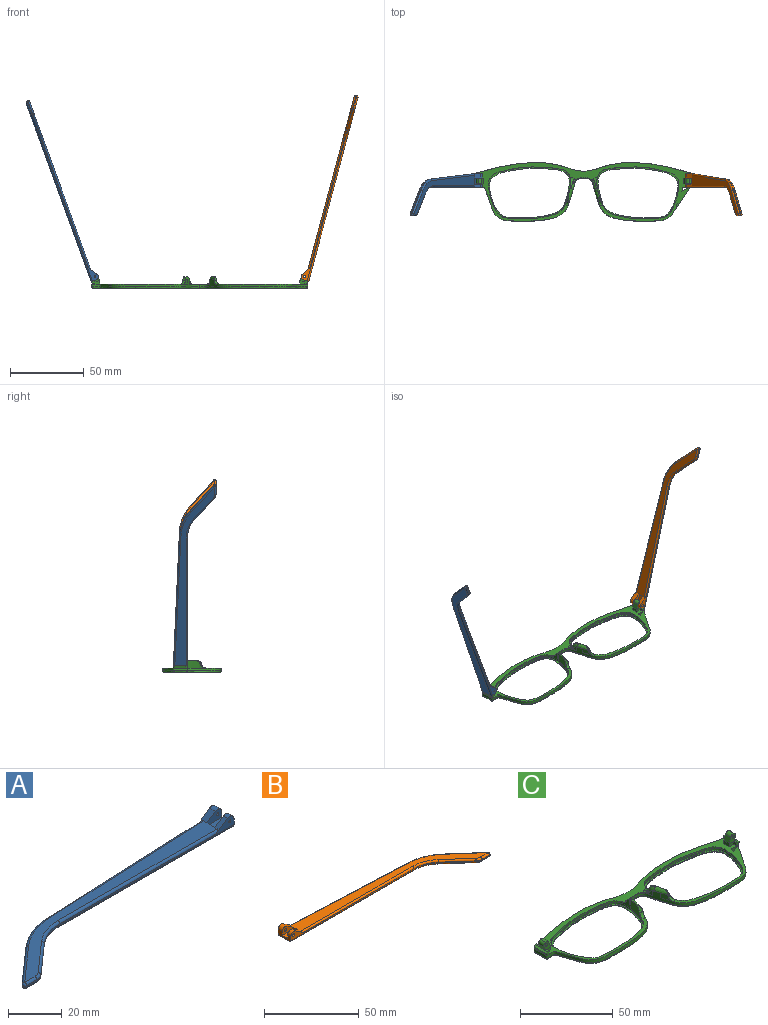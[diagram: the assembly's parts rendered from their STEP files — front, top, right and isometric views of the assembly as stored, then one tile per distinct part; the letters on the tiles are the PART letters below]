
ASSEMBLY  parts=3 mates=2
PART A: 43 faces, bbox 130.2x29.5x5.9 mm
  f0: plane 9.62x3.72mm, normal (1,0,0), area 24.7mm2, adj f1,f3,f4,f5,f10,f16,f18,f28
  f1: cylinder r=2.2mm len=3.45mm, axis (0,-1,0), area 11mm2, adj f0,f2,f4,f37
  f2: plane 6.01x3.91mm, normal (-0.55,0,0.84), area 12.7mm2, adj f1,f4,f9,f19,f37
  f3: plane 2.26x0.1mm, normal (0,0,1), area 0.1mm2, adj f0,f5,f18
  f4: plane 92.1x4.9mm, normal (0,-1,0), area 79.9mm2, adj f0,f1,f2,f14,f19,f36,f42
  f5: plane 93.42x4.13mm, normal (-0.04,1,0), area 64.8mm2, adj f0,f3,f11,f15,f17,f27,f28
  f6: plane 17.82x15.72mm, normal (-0.66,0.75,0), area 14.3mm2, adj f11,f12,f25,f30
  f7: plane 5.46x0.6mm, normal (0,-1,0), area 3.3mm2, adj f12,f13,f23,f32
  f8: plane 14.99x13.23mm, normal (0.66,-0.75,0), area 12mm2, adj f13,f14,f21,f34
  f9: plane 121.18x26.73mm, normal (0,0,1), area 627.7mm2, adj f2,f17,f19,f20,f21,f22,f23,f25
  f10: plane 129.1x27.08mm, normal (0,0,-1), area 686.5mm2, adj f0,f28,f29,f30,f32,f33,f34,f35
  f11: cylinder r=30mm len=18.52mm, axis (0,0,-1), area 12.2mm2, adj f5,f6,f26,f29
  f12: cylinder r=1mm len=1.75mm, axis (0,0,-1), area 1.5mm2, adj f6,f7,f24,f31
  f13: cylinder r=5mm len=3.31mm, axis (0,0,-1), area 2.2mm2, adj f7,f8,f22,f33
  f14: cylinder r=20mm len=13.23mm, axis (0,0,1), area 8.7mm2, adj f4,f8,f20,f35
  f15: plane 5.66x0.25mm, normal (0,0,-1), area 0.7mm2, adj f5,f17,f18
  f16: cylinder r=2.2mm len=3.45mm, axis (0,-1,0), area 14.8mm2, adj f0,f17,f18,f38
  f17: plane 6.01x3.91mm, normal (-0.55,0,0.84), area 16.9mm2, adj f5,f9,f15,f16,f18,f27,f38
  f18: plane 7.92x3.3mm, normal (0,1,0), area 15.9mm2, adj f0,f3,f15,f16,f17,f41
  f19: cylinder r=1mm len=84.18mm, axis (-1,0,0), area 131.4mm2, adj f2,f4,f9,f20
  f20: torus R=21mm, axis (0,0,1), area 23.1mm2, adj f9,f14,f19,f21
  f21: cylinder r=1mm len=15.65mm, axis (-0.75,-0.66,0), area 31.4mm2, adj f8,f9,f20,f22
  f22: torus R=4mm, axis (0,0,1), area 5.3mm2, adj f9,f13,f21,f23
  f23: cylinder r=1mm len=5.46mm, axis (-1,0,0), area 8.6mm2, adj f7,f9,f22,f24
  f24: sphere r=1mm, area 2.4mm2, adj f12,f23,f25
  f25: cylinder r=1mm len=18.48mm, axis (0.75,0.66,0), area 37.3mm2, adj f6,f9,f24,f26
  f26: torus R=29mm, axis (0,0,1), area 31.6mm2, adj f9,f11,f25,f27
  f27: cylinder r=1mm len=85.5mm, axis (1,0.04,0), area 133.5mm2, adj f5,f9,f17,f26
  f28: cylinder r=1mm len=93.46mm, axis (-1,-0.04,0), area 146.9mm2, adj f0,f5,f10,f29
  f29: torus R=29mm, axis (0,0,1), area 31.6mm2, adj f10,f11,f28,f30
  f30: cylinder r=1mm len=18.48mm, axis (-0.75,-0.66,0), area 37.3mm2, adj f6,f10,f29,f31
  f31: sphere r=1mm, area 2.4mm2, adj f12,f30,f32
  f32: cylinder r=1mm len=5.46mm, axis (1,0,0), area 8.6mm2, adj f7,f10,f31,f33
  f33: torus R=4mm, axis (0,0,1), area 5.3mm2, adj f10,f13,f32,f34
  f34: cylinder r=1mm len=15.65mm, axis (0.75,0.66,0), area 31.4mm2, adj f8,f10,f33,f35
  f35: torus R=21mm, axis (0,0,1), area 23.1mm2, adj f10,f14,f34,f36
  f36: cylinder r=1mm len=92.1mm, axis (1,0,0), area 144.7mm2, adj f0,f4,f10,f35
  f37: plane 7.92x4.7mm, normal (0,1,0), area 27mm2, adj f0,f1,f2,f39,f40,f42
  f38: plane 7.92x4.7mm, normal (0,-1,0), area 27mm2, adj f0,f16,f17,f39,f40,f41
  f39: plane 7.92x4.1mm, normal (0,0,1), area 32.5mm2, adj f0,f37,f38,f40
  f40: plane 4.1x1.4mm, normal (1,0,0), area 5.7mm2, adj f9,f37,f38,f39
  f41: cylinder r=0.5mm len=3.1mm, axis (0,-1,0), area 9.7mm2, adj f18,f38
  f42: cylinder r=0.5mm len=2.3mm, axis (0,-1,0), area 7.2mm2, adj f4,f37
PART B: 43 faces, bbox 130.2x29.5x5.9 mm
  f0: plane 9.62x3.72mm, normal (-1,0,0), area 24.7mm2, adj f1,f3,f4,f5,f10,f16,f18,f28
  f1: cylinder r=2.2mm len=3.45mm, axis (0,-1,0), area 11mm2, adj f0,f2,f4,f37
  f2: plane 6.01x3.91mm, normal (0.55,0,0.84), area 12.7mm2, adj f1,f4,f9,f19,f37
  f3: plane 2.26x0.1mm, normal (0,0,1), area 0.1mm2, adj f0,f5,f18
  f4: plane 92.1x4.9mm, normal (0,-1,0), area 78.2mm2, adj f0,f1,f2,f14,f19,f36,f42
  f5: plane 93.42x4.13mm, normal (0.04,1,0), area 64.8mm2, adj f0,f3,f11,f15,f17,f27,f28
  f6: plane 17.82x15.72mm, normal (0.66,0.75,0), area 14.3mm2, adj f11,f12,f25,f30
  f7: plane 5.46x0.6mm, normal (0,-1,0), area 3.3mm2, adj f12,f13,f23,f32
  f8: plane 14.99x13.23mm, normal (-0.66,-0.75,0), area 12mm2, adj f13,f14,f21,f34
  f9: plane 121.18x26.73mm, normal (0,0,1), area 627.7mm2, adj f2,f17,f19,f20,f21,f22,f23,f25
  f10: plane 129.1x27.08mm, normal (0,0,-1), area 686.5mm2, adj f0,f28,f29,f30,f32,f33,f34,f35
  f11: cylinder r=30mm len=18.52mm, axis (0,0,-1), area 12.2mm2, adj f5,f6,f26,f29
  f12: cylinder r=1mm len=1.75mm, axis (0,0,-1), area 1.5mm2, adj f6,f7,f24,f31
  f13: cylinder r=5mm len=3.31mm, axis (0,0,-1), area 2.2mm2, adj f7,f8,f22,f33
  f14: cylinder r=20mm len=13.23mm, axis (0,0,1), area 8.7mm2, adj f4,f8,f20,f35
  f15: plane 5.66x0.25mm, normal (0,0,-1), area 0.7mm2, adj f5,f17,f18
  f16: cylinder r=2.2mm len=3.45mm, axis (0,-1,0), area 14.8mm2, adj f0,f17,f18,f38
  f17: plane 6.01x3.91mm, normal (0.55,0,0.84), area 16.9mm2, adj f5,f9,f15,f16,f18,f27,f38
  f18: plane 7.92x3.3mm, normal (0,1,0), area 14.3mm2, adj f0,f3,f15,f16,f17,f41
  f19: cylinder r=1mm len=84.18mm, axis (1,0,0), area 131.4mm2, adj f2,f4,f9,f20
  f20: torus R=21mm, axis (0,0,1), area 23.1mm2, adj f9,f14,f19,f21
  f21: cylinder r=1mm len=15.65mm, axis (0.75,-0.66,0), area 31.4mm2, adj f8,f9,f20,f22
  f22: torus R=4mm, axis (0,0,1), area 5.3mm2, adj f9,f13,f21,f23
  f23: cylinder r=1mm len=5.46mm, axis (1,0,0), area 8.6mm2, adj f7,f9,f22,f24
  f24: sphere r=1mm, area 2.4mm2, adj f12,f23,f25
  f25: cylinder r=1mm len=18.48mm, axis (-0.75,0.66,0), area 37.3mm2, adj f6,f9,f24,f26
  f26: torus R=29mm, axis (0,0,1), area 31.6mm2, adj f9,f11,f25,f27
  f27: cylinder r=1mm len=85.5mm, axis (-1,0.04,0), area 133.5mm2, adj f5,f9,f17,f26
  f28: cylinder r=1mm len=93.46mm, axis (1,-0.04,0), area 146.9mm2, adj f0,f5,f10,f29
  f29: torus R=29mm, axis (0,0,1), area 31.6mm2, adj f10,f11,f28,f30
  f30: cylinder r=1mm len=18.48mm, axis (0.75,-0.66,0), area 37.3mm2, adj f6,f10,f29,f31
  f31: sphere r=1mm, area 2.4mm2, adj f12,f30,f32
  f32: cylinder r=1mm len=5.46mm, axis (-1,0,0), area 8.6mm2, adj f7,f10,f31,f33
  f33: torus R=4mm, axis (0,0,1), area 5.3mm2, adj f10,f13,f32,f34
  f34: cylinder r=1mm len=15.65mm, axis (-0.75,0.66,0), area 31.4mm2, adj f8,f10,f33,f35
  f35: torus R=21mm, axis (0,0,1), area 23.1mm2, adj f10,f14,f34,f36
  f36: cylinder r=1mm len=92.1mm, axis (-1,0,0), area 144.7mm2, adj f0,f4,f10,f35
  f37: plane 7.92x4.7mm, normal (0,1,0), area 25.4mm2, adj f0,f1,f2,f39,f40,f42
  f38: plane 7.92x4.7mm, normal (0,-1,0), area 25.4mm2, adj f0,f16,f17,f39,f40,f41
  f39: plane 7.92x4.1mm, normal (0,0,1), area 32.5mm2, adj f0,f37,f38,f40
  f40: plane 4.1x1.4mm, normal (-1,0,0), area 5.7mm2, adj f9,f37,f38,f39
  f41: cylinder r=0.88mm len=3.1mm, axis (0,-1,0), area 17mm2, adj f18,f38
  f42: cylinder r=0.88mm len=2.3mm, axis (0,-1,0), area 12.6mm2, adj f4,f37
PART C: 102 faces, bbox 148.1x40.9x17.9 mm
  f0: bspline ~1.82x1.22mm, area 0.7mm2, adj f2,f7,f37,f44
  f1: plane 147.39x40.16mm, normal (0,0,1), area 806.4mm2, adj f4,f5,f6,f7,f8,f12,f20,f23
  f2: bspline ~6.1x4.93mm, area 12.7mm2, adj f0,f7,f37,f41,f43,f44,f45
  f3: plane 4.46x1.45mm, normal (0,0,1), area 0.1mm2, adj f7,f38
  f4: plane 1.23x0.04mm, normal (0,0,1), area 0mm2, adj f1,f7,f22
  f5: plane 6.97x5.07mm, normal (0,1,0), area 22.7mm2, adj f1,f20,f21,f25,f27,f28,f30,f31
  f6: plane 3.2x2.36mm, normal (0,-1,0), area 5.7mm2, adj f1,f20,f26,f29
  f7: extruded ~73.26x39.84mm, area 292.7mm2, adj f0,f1,f2,f3,f4,f8,f13,f14
  f8: extruded ~35.39x5.69mm, area 72.2mm2, adj f1,f7,f18,f59
  f9: plane 144.78x37.85mm, normal (0,0,-1), area 582.4mm2, adj f13,f15,f17,f18,f19,f63,f65,f67
  f10: plane 56.06x35.45mm, normal (0,0,1), area 127mm2, adj f11,f19
  f11: extruded ~55.69x35.36mm, area 160.5mm2, adj f10,f12
  f12: extruded ~55.69x35.36mm, area 231.9mm2, adj f1,f11,f39,f40,f41,f42,f43,f46
  f13: bspline ~73.27x30.39mm, area 161.7mm2, adj f7,f9,f14,f63
  f14: bspline ~1x1mm, area 0.8mm2, adj f7,f13,f15
  f15: bspline ~8.99x1.23mm, area 12.6mm2, adj f7,f9,f14,f16
  f16: bspline ~1.04x1mm, area 0.7mm2, adj f7,f15,f17
  f17: bspline ~45.86x8.59mm, area 59.8mm2, adj f7,f9,f16,f18
  f18: bspline ~37.01x6.7mm, area 56.6mm2, adj f8,f9,f17,f68
  f19: bspline ~56.23x35.9mm, area 235.3mm2, adj f9,f10
  f20: plane 4x2.36mm, normal (-1,0,0), area 9.5mm2, adj f1,f5,f6,f21
  f21: plane 4x0.02mm, normal (0.34,0,0.94), area 0.1mm2, adj f5,f20,f28
  f22: plane 2.76x2.53mm, normal (0,-1,0), area 3.9mm2, adj f4,f26,f27,f35,f48
  f23: plane 7.67x1.6mm, normal (0.94,0,-0.34), area 13mm2, adj f1,f35,f36,f48
  f24: plane 2.1x1.69mm, normal (0,1,0), area 2.8mm2, adj f1,f25,f27,f36,f48
  f25: plane 3.3x2.1mm, normal (-1,0,0), area 6.9mm2, adj f1,f5,f24,f27
  f26: plane 2.35x2.1mm, normal (-1,0,0), area 4.9mm2, adj f1,f6,f22,f27,f29
  f27: plane 9.65x1.24mm, normal (0,0,1), area 8.2mm2, adj f5,f22,f24,f25,f26,f29,f30,f48
  f28: plane 4x3.31mm, normal (-0.94,0,0.34), area 14.1mm2, adj f5,f21,f29,f32
  f29: plane 5.77x5.06mm, normal (0,-1,0), area 17mm2, adj f6,f26,f27,f28,f30,f31,f32,f33
  f30: plane 4x2.21mm, normal (0.94,0,-0.34), area 9.4mm2, adj f5,f27,f29,f33
  f31: plane 4x0.01mm, normal (0.34,0,0.94), area 0mm2, adj f5,f29,f32,f33
  f32: cylinder r=1.98mm len=4mm, axis (0,1,0), area 12.4mm2, adj f5,f28,f29,f31
  f33: cylinder r=1.98mm len=4mm, axis (0,-1,0), area 12.4mm2, adj f5,f29,f30,f31
  f34: cylinder r=0.88mm len=4mm, axis (0,-1,0), area 22mm2, adj f5,f29
  f35: cone r=1mm half-angle=20deg, axis (0,0,1), area 2.3mm2, adj f1,f22,f23,f48
  f36: cylinder r=1mm len=2.28mm, axis (-0.34,0,-0.94), area 3mm2, adj f1,f23,f24,f48
  f37: extruded ~3.67x3.11mm, area 5.9mm2, adj f0,f2,f7,f51
  f38: extruded ~4.44x3.32mm, area 15.1mm2, adj f3,f7,f42,f43,f47
  f39: extruded ~4.98x1.37mm, area 6.6mm2, adj f12,f41
  f40: plane 3.63x0.97mm, normal (0,0,1), area 0.3mm2, adj f12,f41,f43
  f41: bspline ~15.5x15.35mm, area 6.4mm2, adj f2,f12,f39,f40,f46
  f42: bspline ~7.26x7.26mm, area 6.3mm2, adj f12,f38,f43,f47
  f43: bspline ~10.29x4.84mm, area 21.4mm2, adj f2,f7,f12,f38,f40,f42
  f44: bspline ~2.66x2.04mm, area 1.9mm2, adj f0,f2,f7,f45,f50
  f45: bspline ~3.55x3.47mm, area 3.7mm2, adj f1,f2,f44,f46,f50
  f46: bspline ~5.71x4.38mm, area 7.6mm2, adj f1,f12,f41,f45
  f47: bspline ~3.7x3.66mm, area 7.8mm2, adj f1,f7,f12,f38,f42
  f48: plane 9.71x1.44mm, normal (0.34,0,0.94), area 13.9mm2, adj f22,f23,f24,f27,f35,f36
  f49: bspline ~6.38x2.14mm, area 2.6mm2, adj f1,f7,f50,f99
  f50: bspline ~2.1x1.46mm, area 0.6mm2, adj f7,f44,f45,f49
  f51: bspline ~5.24x1.75mm, area 0mm2, adj f7,f37
  f52: bspline ~2.19x1.4mm, area 0.7mm2, adj f53,f58,f87,f94
  f53: bspline ~6.1x4.93mm, area 12.6mm2, adj f52,f58,f87,f91,f93,f94,f95
  f54: plane 4.46x1.45mm, normal (0,0,1), area 0.1mm2, adj f58,f88
  f55: plane 1.23x0.04mm, normal (0,0,1), area 0mm2, adj f1,f58,f72
  f56: plane 6.97x5.07mm, normal (0,1,0), area 22.7mm2, adj f1,f70,f71,f75,f77,f78,f80,f81
  f57: plane 3.2x2.36mm, normal (0,-1,0), area 5.7mm2, adj f1,f70,f76,f79
  f58: extruded ~73.26x39.84mm, area 292.7mm2, adj f1,f7,f52,f53,f54,f55,f59,f63
  f59: extruded ~35.39x5.69mm, area 72.2mm2, adj f1,f8,f58,f68
  f60: plane 56.06x35.45mm, normal (0,0,1), area 127mm2, adj f61,f69
  f61: extruded ~55.69x35.36mm, area 160.5mm2, adj f60,f62
  f62: extruded ~55.69x35.36mm, area 231.9mm2, adj f1,f61,f89,f90,f91,f92,f93,f96
  f63: bspline ~73.83x30.39mm, area 161.7mm2, adj f9,f13,f58,f64
  f64: bspline ~1x1mm, area 0.8mm2, adj f58,f63,f65
  f65: bspline ~8.99x1.23mm, area 12.6mm2, adj f9,f58,f64,f66
  f66: bspline ~1.04x1mm, area 0.8mm2, adj f58,f65,f67
  f67: bspline ~45.86x8.59mm, area 59.8mm2, adj f9,f58,f66,f68
  f68: bspline ~37.01x6.7mm, area 56.6mm2, adj f9,f18,f59,f67
  f69: bspline ~56.22x35.9mm, area 235.3mm2, adj f9,f60
  f70: plane 4x2.36mm, normal (1,0,0), area 9.5mm2, adj f1,f56,f57,f71
  f71: plane 4x0.02mm, normal (-0.34,0,0.94), area 0.1mm2, adj f56,f70,f78
  f72: plane 2.76x2.53mm, normal (0,-1,0), area 3.9mm2, adj f55,f76,f77,f85,f98
  f73: plane 7.67x1.6mm, normal (-0.94,0,-0.34), area 13mm2, adj f1,f85,f86,f98
  f74: plane 2.1x1.69mm, normal (0,1,0), area 2.8mm2, adj f1,f75,f77,f86,f98
  f75: plane 3.3x2.1mm, normal (1,0,0), area 6.9mm2, adj f1,f56,f74,f77
  f76: plane 2.35x2.1mm, normal (1,0,0), area 4.9mm2, adj f1,f57,f72,f77,f79
  f77: plane 9.65x1.24mm, normal (0,0,1), area 8.2mm2, adj f56,f72,f74,f75,f76,f79,f80,f98
  f78: plane 4x3.31mm, normal (0.94,0,0.34), area 14.1mm2, adj f56,f71,f79,f82
  f79: plane 5.77x5.06mm, normal (0,-1,0), area 17mm2, adj f57,f76,f77,f78,f80,f81,f82,f83
  f80: plane 4x2.21mm, normal (-0.94,0,-0.34), area 9.4mm2, adj f56,f77,f79,f83
  f81: plane 4x0.01mm, normal (-0.34,0,0.94), area 0mm2, adj f56,f79,f82,f83
  f82: cylinder r=1.98mm len=4mm, axis (0,1,0), area 12.4mm2, adj f56,f78,f79,f81
  f83: cylinder r=1.98mm len=4mm, axis (0,-1,0), area 12.4mm2, adj f56,f79,f80,f81
  f84: cylinder r=0.88mm len=4mm, axis (0,-1,0), area 22mm2, adj f56,f79
  f85: cone r=1mm half-angle=20deg, axis (0,0,1), area 2.3mm2, adj f1,f72,f73,f98
  f86: cylinder r=1mm len=2.28mm, axis (0.34,0,-0.94), area 3mm2, adj f1,f73,f74,f98
  f87: extruded ~3.67x3.11mm, area 5.9mm2, adj f52,f53,f58,f101
  f88: extruded ~4.44x3.32mm, area 15.1mm2, adj f54,f58,f92,f93,f97
  f89: extruded ~4.98x1.36mm, area 6.6mm2, adj f62,f91
  f90: plane 3.63x0.97mm, normal (0,0,1), area 0.3mm2, adj f62,f91,f93
  f91: bspline ~15.5x15.35mm, area 6.4mm2, adj f53,f62,f89,f90,f96
  f92: bspline ~7.26x7.26mm, area 6.2mm2, adj f62,f88,f93,f97
  f93: bspline ~10.29x4.84mm, area 21.5mm2, adj f53,f58,f62,f88,f90,f92
  f94: bspline ~2.65x2.03mm, area 1.9mm2, adj f52,f53,f58,f95,f100
  f95: bspline ~3.55x3.47mm, area 3.7mm2, adj f1,f53,f94,f96,f100
  f96: bspline ~5.57x4.33mm, area 7.6mm2, adj f1,f62,f91,f95
  f97: bspline ~3.7x3.66mm, area 7.8mm2, adj f1,f58,f62,f88,f92
  f98: plane 9.71x1.44mm, normal (-0.34,0,0.94), area 13.9mm2, adj f72,f73,f74,f77,f85,f86
  f99: bspline ~6.38x2.14mm, area 2.6mm2, adj f1,f49,f58,f100
  f100: bspline ~2.1x1.46mm, area 0.6mm2, adj f58,f94,f95,f99
  f101: bspline ~5.24x1.75mm, area 0mm2, adj f58,f87
PLACE A rot(axis=(0,1,0),70deg) t=(-84.77,-5.75,56)mm
PLACE B rot(axis=(0,-1,0),75deg) t=(68.2,-5.75,-61.61)mm
PLACE C t=(10.15,-1.13,-5.77)mm
MATE revolute A.f1 <-> C.f82  axis (0,-1,0) through (-60.89,2.72,1.22)mm
MATE revolute B.f41 <-> C.f33  axis (0,-1,0) through (81.2,2.72,1.21)mm
